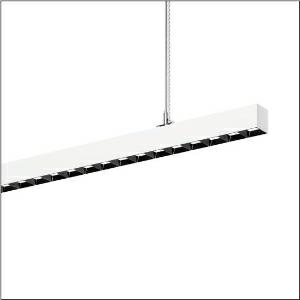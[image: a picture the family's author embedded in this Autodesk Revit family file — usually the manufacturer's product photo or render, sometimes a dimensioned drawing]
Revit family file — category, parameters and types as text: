
# Revit family: silica_r__21_51mx32tat7w_976d
name_source: partatom
category: Lighting Fixtures
units: mm (PartAtom-declared; Revit-internal decimal feet)

## family parameters
Cut with Voids When Loaded = No
Host = Face
Light Source = No
Part Type = Normal
Room Calculation Point = No
Round Connector Dimension = Use Diameter
Shared = No

## types (1)
- --- (1 x LED, 6220 lm, 53.4 W, 6500K)
    Apparent Load = 53 VA
    CIE Flux Codes = 84 99 100 60 100
    Color Rendering = 80
    Color Temperature = 6500K
    Default Elevation = 1800 mm
    Description = Silica® 21, office luminaire, primary light control with darklight reflector, of PMMA, black, CAT 2 (L<= 3000cd/m²), light emission: direct/indirect distribution, primary light characteristic: symmetric, installation type: suspended mounting, LED, rated luminous flux: 6.220lm, luminous efficacy: 111lm/W, light colour: 8tw, colour temperature: 2700..6500K, control gear: DALI DT8, with terminal, 3+2-pole, max. 2.5mm², mains connection: 220..240V, AC, 50/60Hz, rated input power: 56.1W, luminaire housing, of aluminium, traffic white (RAL 9016), length: 1.204mm, width: 53mm, height: 53mm, protection rating (complete): IP20, insulation class (complete): insulation class I (protective earthing), certification: CE, permissible operating ambient temperature: 0..+35°C, standard: EN 50419, packaging unit: 1 piece
    Height = 53 mm
    Lamp = 1 x LED
    Lamp Light Flux = 6220 lm
    Lamp Power = 53.4 W
    Lamp count = 1
    Length = 1204 mm
    Luminous efficacy = 116 lm/W
    Manufacturer = Siteco
    ModVariant = No
    Model = 51MX32TAT7W
    Mounting Place = Ceiling
    Mounting Type = Pendant
    Number of Poles = 1
    OnlyDefault = Yes
    Power Factor = 1
    Product Name = Silica® 21
    Product group = office luminaire | ceiling pendant
    ProductGroupID = 904
    Protection Class = Protection class I
    Protection Degree = IP 20
    RLX_Detail_Level = 1
    RLX_Emergency_Light_Flux = 0 lm
    RLX_Emergency_Type = 0
    RLX_Emergency_Type_DB = No
    RlxData = <blob elided: 40181 chars, md5=17eb7bb7>
    Socket = socket
    Standby Power = 0 W
    System Light Flux = 6220 lm
    System Power = 53 W
    Type Comments = individual setting
    Type Image = l_1335871.jpg
    URL = http://relux.com
    VarID = @adj_139962
    Voltage = 0 V
    Weight = 0.00 kg
    Width = 53 mm

## geometry (parser evidence)
native form markers: Blend x4, Sweep x14
no freeform markers — native parametric forms only
